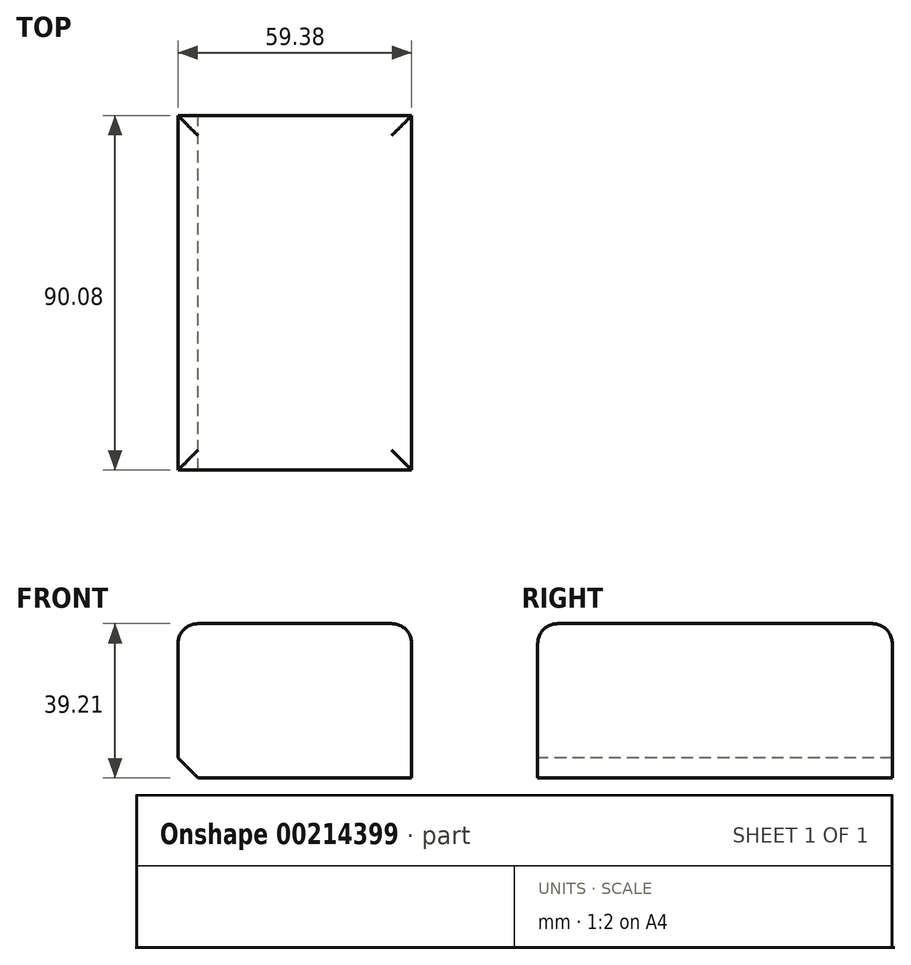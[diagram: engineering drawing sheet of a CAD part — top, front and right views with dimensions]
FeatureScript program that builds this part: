
annotation { "Feature Type Name" : "Feature", "Feature Type Description" : "" }
export const myFeature = defineFeature(function(context is Context, id is Id, definition is map)
    precondition{}
    {
        {
            var Q0;
            Q0=qCreatedBy(makeId("Front.planeOp"),FACE);
            var sketch = newSketch(context, id + "F0", { "sketchPlane" : qUnion([Q0])});
            skLineSegment(sketch, "E0.bottom", {"start": v(0, 0) * mm, "end": v(59.38, 0) * mm});
            skLineSegment(sketch, "E0.top", {"start": v(0, -39.2) * mm, "end": v(59.38, -39.2) * mm});
            skLineSegment(sketch, "E0.left", {"start": v(0, 0) * mm, "end": v(0, -39.2) * mm});
            skLineSegment(sketch, "E0.right", {"start": v(59.38, 0) * mm, "end": v(59.38, -39.2) * mm});
            skSolve(sketch);
        }
        {
            var Q0;
            Q0 = qSketchRegion(id + "F0", true);
            extrude(context, id + "F1", {"entities" : qUnion([Q0]), "depth" : 90.08 * mm});
        }
        {
            var Q0;
            Q0=makeQuery(id+"F1.opExtrude","SWEPT_EDGE",EDGE,{"disambiguationData":[OSD([sQuery(id+"F0.wireOp",EDGE,"E0.bottom"),sQuery(id+"F0.wireOp",EDGE,"E0.right")])]});
            var Q1;
            Q1=makeQuery(id+"F1.opExtrude","SWEPT_FACE",FACE,{"disambiguationData":[OSD([sQuery(id+"F0.wireOp",EDGE,"E0.bottom")])]});
            fillet(context, id + "F3", {"entities" : qUnion([Q0, Q1]), "radius" : 5.08 * mm, "tangentPropagation" : true, "allowEdgeOverflow" : false});
        }
        {
            var Q0;
            Q0=makeQuery(id+"F1.opExtrude","SWEPT_EDGE",EDGE,{"disambiguationData":[OSD([sQuery(id+"F0.wireOp",EDGE,"E0.top"),sQuery(id+"F0.wireOp",EDGE,"E0.left")])]});
            chamfer(context, id + "F2", {"entities" : qUnion([Q0]), "width" : 5.08 * mm, "tangentPropagation" : true});
        }
    });
